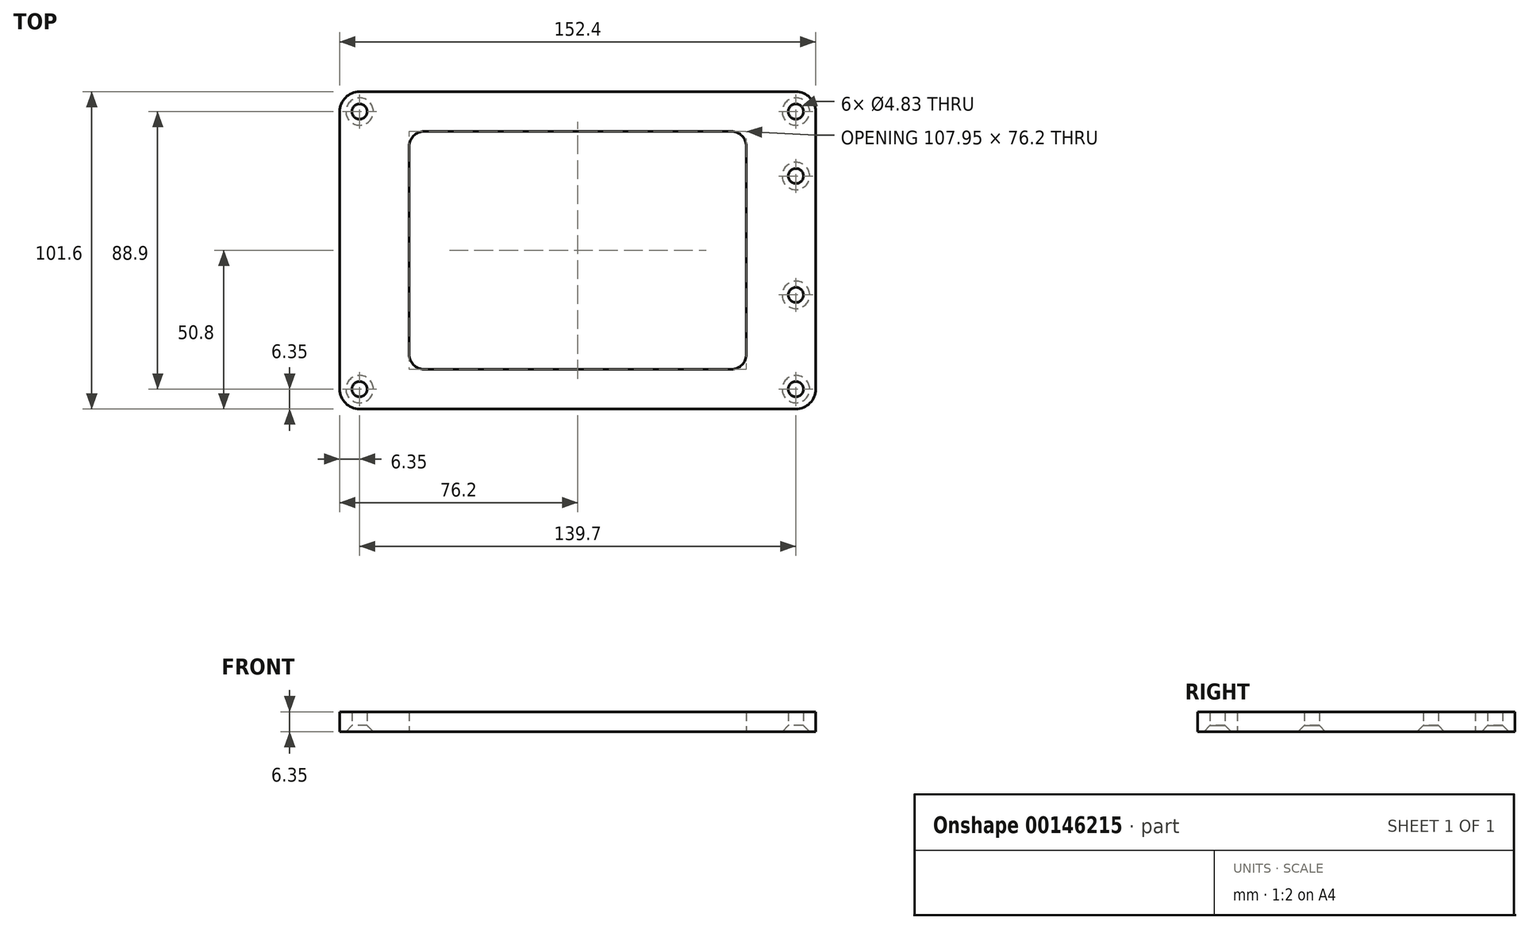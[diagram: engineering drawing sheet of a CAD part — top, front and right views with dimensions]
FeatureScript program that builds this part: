
annotation { "Feature Type Name" : "Feature", "Feature Type Description" : "" }
export const myFeature = defineFeature(function(context is Context, id is Id, definition is map)
    precondition{}
    {
        {
            var Q0;
            Q0=qCreatedBy(makeId("Top.planeOp"),FACE);
            var sketch = newSketch(context, id + "F0", { "sketchPlane" : qUnion([Q0])});
            skLineSegment(sketch, "E0.bottom", {"start": v(-69.85, -50.8) * mm, "end": v(69.85, -50.8) * mm});
            skLineSegment(sketch, "E0.top", {"start": v(-69.85, 50.8) * mm, "end": v(69.85, 50.8) * mm});
            skLineSegment(sketch, "E0.left", {"start": v(-76.2, -44.45) * mm, "end": v(-76.2, 44.45) * mm});
            skLineSegment(sketch, "E0.right", {"start": v(76.2, -44.45) * mm, "end": v(76.2, 44.45) * mm});
            skPoint(sketch, "E0.middle", {"position": v(0, 0) * mm});
            skPoint(sketch, "E1.visualSharp", {"position": v(-76.2, 50.8) * mm});
            skArc(sketch, "E1.filletArc", {"start": v(-69.85, 50.8) * mm, "mid": v(-74.34, 48.94) * mm, "end": v(-76.2, 44.45) * mm});
            skPoint(sketch, "E2.visualSharp", {"position": v(-76.2, -50.8) * mm});
            skArc(sketch, "E2.filletArc", {"start": v(-76.2, -44.45) * mm, "mid": v(-74.34, -48.94) * mm, "end": v(-69.85, -50.8) * mm});
            skPoint(sketch, "E3.visualSharp", {"position": v(76.2, 50.8) * mm});
            skArc(sketch, "E3.filletArc", {"start": v(76.2, 44.45) * mm, "mid": v(74.34, 48.94) * mm, "end": v(69.85, 50.8) * mm});
            skPoint(sketch, "E4.visualSharp", {"position": v(76.2, -50.8) * mm});
            skArc(sketch, "E4.filletArc", {"start": v(69.85, -50.8) * mm, "mid": v(74.34, -48.94) * mm, "end": v(76.2, -44.45) * mm});
            skLineSegment(sketch, "E5.bottom", {"start": v(-49.2, 38.1) * mm, "end": v(49.2, 38.1) * mm});
            skLineSegment(sketch, "E5.top", {"start": v(-49.2, -38.1) * mm, "end": v(49.2, -38.1) * mm});
            skLineSegment(sketch, "E5.left", {"start": v(-53.98, 33.32) * mm, "end": v(-53.98, -33.32) * mm});
            skLineSegment(sketch, "E5.right", {"start": v(53.97, 33.32) * mm, "end": v(53.97, -33.32) * mm});
            skPoint(sketch, "E6.visualSharp", {"position": v(-53.98, 38.1) * mm});
            skArc(sketch, "E6.filletArc", {"start": v(-49.2, 38.1) * mm, "mid": v(-52.58, 36.7) * mm, "end": v(-53.98, 33.32) * mm});
            skPoint(sketch, "E7.visualSharp", {"position": v(53.97, 38.1) * mm});
            skArc(sketch, "E7.filletArc", {"start": v(53.97, 33.32) * mm, "mid": v(52.58, 36.7) * mm, "end": v(49.2, 38.1) * mm});
            skPoint(sketch, "E8.visualSharp", {"position": v(53.97, -38.1) * mm});
            skArc(sketch, "E8.filletArc", {"start": v(49.2, -38.1) * mm, "mid": v(52.58, -36.7) * mm, "end": v(53.97, -33.32) * mm});
            skPoint(sketch, "E9.visualSharp", {"position": v(-53.98, -38.1) * mm});
            skArc(sketch, "E9.filletArc", {"start": v(-53.98, -33.32) * mm, "mid": v(-52.58, -36.7) * mm, "end": v(-49.2, -38.1) * mm});
            skCircle(sketch, "E10", {"center": v(-69.85, 44.45) * mm, "radius": 2.41 * mm});
            skCircle(sketch, "E11.MirrorC", {"center": v(-69.85, -44.45) * mm, "radius": 2.41 * mm});
            skCircle(sketch, "E12.MirrorC", {"center": v(69.85, 44.45) * mm, "radius": 2.41 * mm});
            skCircle(sketch, "E13.MirrorC", {"center": v(69.85, -44.45) * mm, "radius": 2.41 * mm});
            skCircle(sketch, "E14", {"center": v(69.85, 23.81) * mm, "radius": 2.41 * mm});
            skCircle(sketch, "E15", {"center": v(69.85, -14.27) * mm, "radius": 2.41 * mm});
            skLineSegment(sketch, "E16", {"start": v(-76.2, 0) * mm, "end": v(76.2, 0) * mm, "construction": true});
            skSolve(sketch);
        }
        {
            var Q0;
            Q0 = qSketchRegion(id + "F0", true);
            extrude(context, id + "F1", {"entities" : qUnion([Q0]), "depth" : 6.35 * mm});
        }
        {
            var Q0;
            Q0=makeQuery(id+"F1.opExtrude","CAP_EDGE",EDGE,{"disambiguationData":[OSD([sQuery(id+"F0.wireOp",EDGE,"E10")])],"isStart":true});
            var Q1;
            Q1=makeQuery(id+"F1.opExtrude","CAP_EDGE",EDGE,{"disambiguationData":[OSD([sQuery(id+"F0.wireOp",EDGE,"E11.MirrorC")])],"isStart":true});
            var Q2;
            Q2=makeQuery(id+"F1.opExtrude","CAP_EDGE",EDGE,{"disambiguationData":[OSD([sQuery(id+"F0.wireOp",EDGE,"E12.MirrorC")])],"isStart":true});
            var Q3;
            Q3=makeQuery(id+"F1.opExtrude","CAP_EDGE",EDGE,{"disambiguationData":[OSD([sQuery(id+"F0.wireOp",EDGE,"E13.MirrorC")])],"isStart":true});
            chamfer(context, id + "F2", {"entities" : qUnion([Q0, Q1, Q2, Q3]), "width" : 1.98 * mm, "tangentPropagation" : true});
        }
        {
            var Q0;
            Q0=makeQuery(id+"F1.opExtrude","CAP_EDGE",EDGE,{"disambiguationData":[OSD([sQuery(id+"F0.wireOp",EDGE,"E14")])],"isStart":true});
            var Q1;
            Q1=makeQuery(id+"F1.opExtrude","CAP_EDGE",EDGE,{"disambiguationData":[OSD([sQuery(id+"F0.wireOp",EDGE,"E15")])],"isStart":true});
            chamfer(context, id + "F3", {"entities" : qUnion([Q0, Q1]), "width" : 1.98 * mm, "tangentPropagation" : true});
        }
    });
